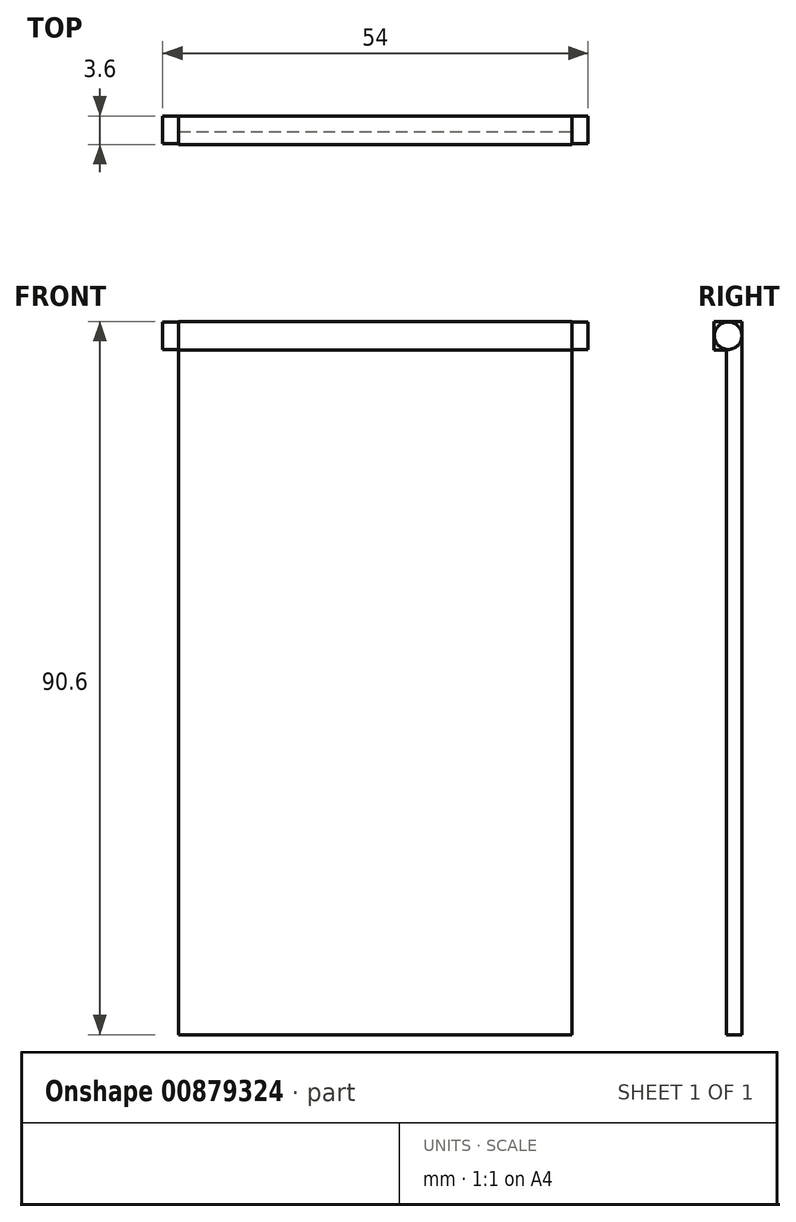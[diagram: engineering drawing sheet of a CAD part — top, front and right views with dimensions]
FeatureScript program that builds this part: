
annotation { "Feature Type Name" : "Feature", "Feature Type Description" : "" }
export const myFeature = defineFeature(function(context is Context, id is Id, definition is map)
    precondition{}
    {
        {
            var Q0;
            Q0=qCreatedBy(makeId("Front.planeOp"),FACE);
            var sketch = newSketch(context, id + "F0", { "sketchPlane" : qUnion([Q0])});
            skLineSegment(sketch, "E0.bottom", {"start": v(0, 0) * mm, "end": v(50, 0) * mm});
            skLineSegment(sketch, "E0.top", {"start": v(0, 81) * mm, "end": v(50, 81) * mm});
            skLineSegment(sketch, "E0.left", {"start": v(0, 0) * mm, "end": v(0, 81) * mm});
            skLineSegment(sketch, "E0.right", {"start": v(50, 0) * mm, "end": v(50, 81) * mm});
            skLineSegment(sketch, "E1", {"start": v(0, 81) * mm, "end": v(0, 84.6) * mm});
            skLineSegment(sketch, "E2", {"start": v(0, 84.6) * mm, "end": v(50, 84.6) * mm});
            skLineSegment(sketch, "E3", {"start": v(50, 84.6) * mm, "end": v(50, 81) * mm});
            skSolve(sketch);
        }
        {
            var Q0;
            Q0=makeQuery(id+"F0.imprint","IMPRINT",FACE,{"disambiguationData":[TD([[makeQuery(id+"F0.imprint","IMPRINT",EDGE,{"derivedFrom":sQuery(id+"F0.wireOp",EDGE,"E0.bottom")}),1.0]])]});
            extrude(context, id + "F1", {"entities" : qUnion([Q0]), "depth" : 2 * mm, "offsetDistance" : 25 * mm});
        }
        {
            var Q0;
            Q0=makeQuery(id+"F0.imprint","IMPRINT",FACE,{"disambiguationData":[TD([[makeQuery(id+"F0.imprint","IMPRINT",EDGE,{"derivedFrom":sQuery(id+"F0.wireOp",EDGE,"E0.top")}),1.0]])]});
            extrude(context, id + "F2", {"entities" : qUnion([Q0]), "operationType" : NewBodyOperationType.ADD, "depth" : 3.6 * mm, "offsetDistance" : 25 * mm});
        }
        {
            var Q0;
            Q0=makeQuery(id+"F2.boolean.opBoolean","MERGE",FACE,{"derivedFrom":[makeQuery(id+"F1.opExtrude","SWEPT_FACE",FACE,{"disambiguationData":[OSD([sQuery(id+"F0.wireOp",EDGE,"E0.right")])]}),makeQuery(id+"F2.opExtrude","SWEPT_FACE",FACE,{"disambiguationData":[OSD([sQuery(id+"F0.wireOp",EDGE,"E3")])]})]});
            var sketch = newSketch(context, id + "F3", { "sketchPlane" : qUnion([Q0])});
            skLineSegment(sketch, "E4", {"start": v(-3.6, 82.8) * mm, "end": v(-1.78, 82.8) * mm, "construction": true});
            skCircle(sketch, "E5", {"center": v(-1.78, 82.8) * mm, "radius": 1.75 * mm});
            skSolve(sketch);
        }
        {
            var Q0;
            Q0=makeQuery(id+"F2.boolean.opBoolean","MERGE",FACE,{"derivedFrom":[makeQuery(id+"F1.opExtrude","SWEPT_FACE",FACE,{"disambiguationData":[OSD([sQuery(id+"F0.wireOp",EDGE,"E0.left")])]}),makeQuery(id+"F2.opExtrude","SWEPT_FACE",FACE,{"disambiguationData":[OSD([sQuery(id+"F0.wireOp",EDGE,"E1")])]})]});
            var sketch = newSketch(context, id + "F4", { "sketchPlane" : qUnion([Q0])});
            skLineSegment(sketch, "E6", {"start": v(3.6, 82.8) * mm, "end": v(1.78, 82.8) * mm, "construction": true});
            skCircle(sketch, "E7", {"center": v(1.78, 82.8) * mm, "radius": 1.75 * mm});
            skSolve(sketch);
        }
        {
            var Q0;
            Q0=makeQuery(id+"F4.imprint","IMPRINT",FACE,{"disambiguationData":[TD([[makeQuery(id+"F4.imprint","IMPRINT",EDGE,{"derivedFrom":sQuery(id+"F4.wireOp",EDGE,"E7")}),1.0]])]});
            extrude(context, id + "F5", {"entities" : qUnion([Q0]), "operationType" : NewBodyOperationType.ADD, "depth" : 2 * mm, "offsetDistance" : 25 * mm});
        }
        {
            var Q0;
            Q0=makeQuery(id+"F3.imprint","IMPRINT",FACE,{"disambiguationData":[TD([[makeQuery(id+"F3.imprint","IMPRINT",EDGE,{"derivedFrom":sQuery(id+"F3.wireOp",EDGE,"E5")}),1.0]])]});
            extrude(context, id + "F6", {"entities" : qUnion([Q0]), "operationType" : NewBodyOperationType.ADD, "depth" : 2 * mm, "offsetDistance" : 25 * mm});
        }
        {
            var Q0;
            Q0=makeQuery(id+"F1.opExtrude","SWEPT_FACE",FACE,{"disambiguationData":[OSD([sQuery(id+"F0.wireOp",EDGE,"E0.bottom")])]});
            extrude(context, id + "F7", {"entities" : qUnion([Q0]), "operationType" : NewBodyOperationType.ADD, "depth" : 6 * mm, "offsetDistance" : 25 * mm});
        }
    });
